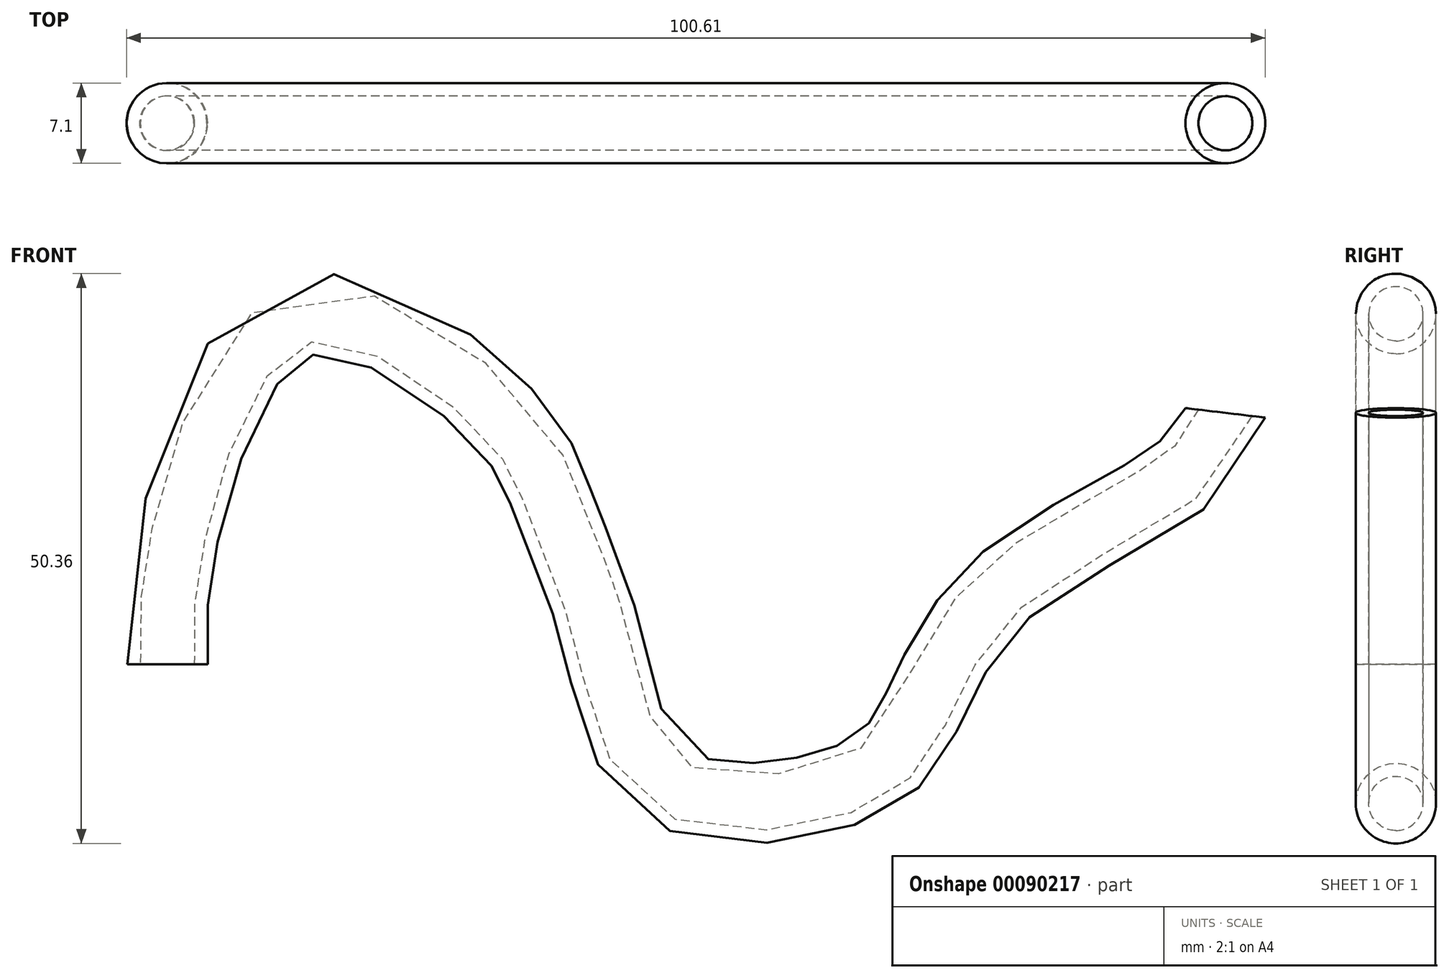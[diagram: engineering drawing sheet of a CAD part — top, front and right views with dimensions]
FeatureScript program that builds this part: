
annotation { "Feature Type Name" : "Feature", "Feature Type Description" : "" }
export const myFeature = defineFeature(function(context is Context, id is Id, definition is map)
    precondition{}
    {
        {
            var Q0;
            Q0=qCreatedBy(makeId("Front.planeOp"),FACE);
            var sketch = newSketch(context, id + "F0", { "sketchPlane" : qUnion([Q0])});
            skPoint(sketch, "E0", {"position": v(-44.54, 0) * mm});
            skPoint(sketch, "E1", {"position": v(-43.26, 12.92) * mm});
            skPoint(sketch, "E2", {"position": v(-32.44, 31.07) * mm});
            skPoint(sketch, "E3", {"position": v(-13.56, 21.17) * mm});
            skPoint(sketch, "E4", {"position": v(-9.71, 13.84) * mm});
            skPoint(sketch, "E5", {"position": v(-5.68, 2.84) * mm});
            skPoint(sketch, "E6", {"position": v(0, -10.36) * mm});
            skPoint(sketch, "E7", {"position": v(15.76, -10.36) * mm});
            skPoint(sketch, "E8", {"position": v(21.45, -5.4) * mm});
            skPoint(sketch, "E9", {"position": v(30.06, 7.6) * mm});
            skPoint(sketch, "E10", {"position": v(48.94, 22.27) * mm});
            skFitSpline(sketch, "E11", {"points": [v(-44.54, 0) * mm, v(-43.26, 12.92) * mm, v(-32.44, 31.07) * mm, v(-13.56, 21.17) * mm, v(-9.71, 13.84) * mm, v(-5.68, 2.84) * mm, v(0, -10.36) * mm, v(15.76, -10.36) * mm, v(21.45, -5.4) * mm, v(30.06, 7.6) * mm, v(48.94, 22.27) * mm], "startDerivative": vector(-7.13, 144.14) * mm, "endDerivative": vector(9.48, 138.33) * mm});
            skSolve(sketch);
        }
        {
            var Q0;
            Q0=qCreatedBy(makeId("Top.planeOp"),FACE);
            var sketch = newSketch(context, id + "F1", { "sketchPlane" : qUnion([Q0])});
            skCircle(sketch, "E12", {"center": v(-44.24, 0) * mm, "radius": 3.55 * mm});
            skCircle(sketch, "E13", {"center": v(-44.24, 0) * mm, "radius": 2.4 * mm});
            skSolve(sketch);
        }
        {
            var Q0;
            Q0=makeQuery(id+"F1.imprint","IMPRINT",FACE,{"disambiguationData":[TD([[makeQuery(id+"F1.imprint","IMPRINT",EDGE,{"derivedFrom":sQuery(id+"F1.wireOp",EDGE,"E12")}),1.0]])]});
            var Q1;
            Q1=sQuery(id+"F0.wireOp",EDGE,"E11");
            sweep(context, id + "F2", {"profiles" : qUnion([Q0]), "path" : qUnion([Q1])});
        }
        {
            var Q0;
            Q0=qCreatedBy(makeId("Right.planeOp"),FACE);
            var sketch = newSketch(context, id + "F3", { "sketchPlane" : qUnion([Q0])});
            skPoint(sketch, "E14", {"position": v(-43.26, 31.99) * mm});
            skPoint(sketch, "E15", {"position": v(-35.56, 45.92) * mm});
            skPoint(sketch, "E16", {"position": v(-15.4, 53.61) * mm});
            skPoint(sketch, "E17", {"position": v(18.7, 44.82) * mm});
            skPoint(sketch, "E18", {"position": v(5.5, 51.97) * mm});
            skFitSpline(sketch, "E19", {"points": [v(-43.26, 31.99) * mm, v(-35.56, 45.92) * mm, v(-15.4, 53.61) * mm, v(5.5, 51.97) * mm, v(18.7, 44.82) * mm], "startDerivative": vector(23.33, 65.62) * mm, "endDerivative": vector(53.8, -36.08) * mm});
            skSolve(sketch);
        }
    });
